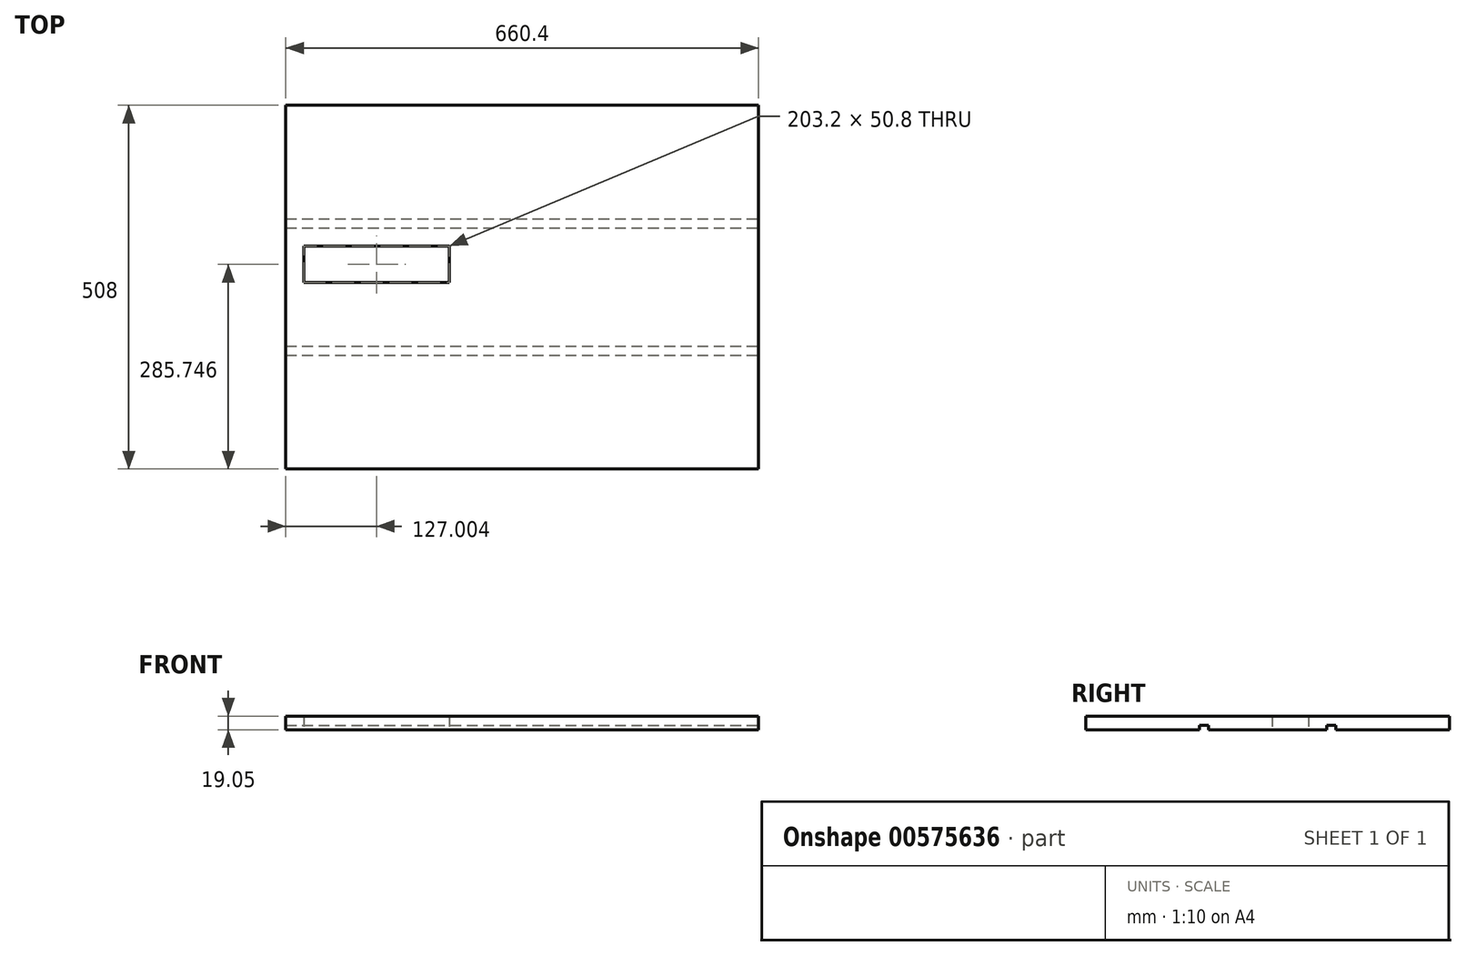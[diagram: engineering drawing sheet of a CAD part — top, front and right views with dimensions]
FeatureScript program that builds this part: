
annotation { "Feature Type Name" : "Feature", "Feature Type Description" : "" }
export const myFeature = defineFeature(function(context is Context, id is Id, definition is map)
    precondition{}
    {
        {
            var Q0;
            Q0=qCreatedBy(makeId("Top.planeOp"),FACE);
            var sketch = newSketch(context, id + "F0", { "sketchPlane" : qUnion([Q0])});
            skLineSegment(sketch, "E0.bottom", {"start": v(-46.34, 447.39) * mm, "end": v(614.06, 447.39) * mm});
            skLineSegment(sketch, "E0.top", {"start": v(-46.34, -60.61) * mm, "end": v(614.06, -60.61) * mm});
            skLineSegment(sketch, "E0.left", {"start": v(-46.34, 447.39) * mm, "end": v(-46.34, -60.61) * mm});
            skLineSegment(sketch, "E0.right", {"start": v(614.06, 447.39) * mm, "end": v(614.06, 415.64) * mm});
            skPoint(sketch, "E1.orphan", {"position": v(283.86, -60.61) * mm});
            skPoint(sketch, "E2.orphan", {"position": v(283.86, 447.39) * mm});
            skLineSegment(sketch, "E3.trimOffspring", {"start": v(614.06, 396.59) * mm, "end": v(614.06, -9.81) * mm});
            skLineSegment(sketch, "E4.trimOffspring", {"start": v(614.06, -28.86) * mm, "end": v(614.06, -60.61) * mm});
            skPoint(sketch, "E5.orphan", {"position": v(614.06, 193.39) * mm});
            skLineSegment(sketch, "E6", {"start": v(614.06, -9.81) * mm, "end": v(614.06, -28.86) * mm});
            skLineSegment(sketch, "E7", {"start": v(614.06, 396.59) * mm, "end": v(614.06, 415.64) * mm});
            skLineSegment(sketch, "E8", {"start": v(283.86, 447.39) * mm, "end": v(283.86, -60.61) * mm, "construction": true});
            skLineSegment(sketch, "E9.MirrorCS", {"start": v(182.26, 250.54) * mm, "end": v(182.26, 199.74) * mm});
            skLineSegment(sketch, "E10.MirrorCS", {"start": v(-20.94, 250.54) * mm, "end": v(182.26, 250.54) * mm});
            skLineSegment(sketch, "E11.MirrorCS", {"start": v(182.26, 199.74) * mm, "end": v(-20.94, 199.74) * mm});
            skLineSegment(sketch, "E12.MirrorCS", {"start": v(-20.94, 250.54) * mm, "end": v(-20.94, 199.74) * mm});
            skSolve(sketch);
        }
        {
            var Q0;
            Q0=qSketchRegion(id+"F0",true);
            extrude(context, id + "F1", {"entities" : qUnion([Q0]), "depth" : 19.05 * mm, "offsetDistance" : 25.4 * mm});
        }
        {
            var Q0;
            Q0=makeQuery(id+"F1.opExtrude","CAP_FACE",FACE,{"disambiguationData":[OSD([sQuery(id+"F0.wireOp",EDGE,"E0.bottom"),sQuery(id+"F0.wireOp",EDGE,"E0.top"),sQuery(id+"F0.wireOp",EDGE,"E0.left"),sQuery(id+"F0.wireOp",EDGE,"E0.right"),sQuery(id+"F0.wireOp",EDGE,"E3.trimOffspring"),sQuery(id+"F0.wireOp",EDGE,"E4.trimOffspring"),sQuery(id+"F0.wireOp",EDGE,"i5BfIIhn-vbHe-imx1-csDb-nMQiqM2HRBRM.top"),sQuery(id+"F0.wireOp",EDGE,"i5BfIIhn-vbHe-imx1-csDb-nMQiqM2HRBRM.right"),sQuery(id+"F0.wireOp",EDGE,"78bbb6ff-89c4-4b25-9ef8-bd1ca9e1b5700.MirrorCS"),sQuery(id+"F0.wireOp",EDGE,"78bbb6ff-89c4-4b25-9ef8-bd1ca9e1b5701.MirrorCS"),sQuery(id+"F0.wireOp",EDGE,"ff8e6387-9dfd-4042-92c4-0e13fc46f2381.MirrorCS"),sQuery(id+"F0.wireOp",EDGE,"ff8e6387-9dfd-4042-92c4-0e13fc46f2382.MirrorCS"),sQuery(id+"F0.wireOp",EDGE,"lPivuiSJ-rouK-T9NZ-5f0i-5M2m3eOQRDiC"),sQuery(id+"F0.wireOp",EDGE,"E6"),sQuery(id+"F0.wireOp",EDGE,"E7")])],"isStart":true});
            var sketch = newSketch(context, id + "F2", { "sketchPlane" : qUnion([Q0])});
            skLineSegment(sketch, "E13.bottom", {"start": v(-46.34, 60.61) * mm, "end": v(614.06, 60.61) * mm});
            skLineSegment(sketch, "E13.top", {"start": v(-46.34, -447.39) * mm, "end": v(614.06, -447.39) * mm});
            skLineSegment(sketch, "E13.left", {"start": v(-46.34, -98.14) * mm, "end": v(-46.34, -110.84) * mm});
            skLineSegment(sketch, "E13.right", {"start": v(614.06, -98.14) * mm, "end": v(614.06, -110.84) * mm});
            skLineSegment(sketch, "E14.0", {"start": v(4.46, -282.29) * mm, "end": v(614.06, -282.29) * mm, "construction": true});
            skLineSegment(sketch, "E15.0", {"start": v(-46.34, -104.49) * mm, "end": v(563.26, -104.49) * mm, "construction": true});
            skLineSegment(sketch, "E16.0", {"start": v(-46.34, -110.84) * mm, "end": v(614.06, -110.84) * mm});
            skLineSegment(sketch, "E17.0", {"start": v(-46.34, -98.14) * mm, "end": v(614.06, -98.14) * mm});
            skLineSegment(sketch, "E18.0", {"start": v(-46.34, -288.64) * mm, "end": v(614.06, -288.64) * mm});
            skLineSegment(sketch, "E19.0", {"start": v(-46.34, -275.94) * mm, "end": v(614.06, -275.94) * mm});
            skLineSegment(sketch, "E20.trimOffspring", {"start": v(614.06, -275.94) * mm, "end": v(614.06, -288.64) * mm});
            skLineSegment(sketch, "E21.trimOffspring", {"start": v(-46.34, -275.94) * mm, "end": v(-46.34, -288.64) * mm});
            skSolve(sketch);
        }
        {
            var Q0;
            {var subQ1=sQuery(id+"F2.wireOp",EDGE,"ede1b310-70a5-4bce-ad08-636cf6eacef5.0");Q0=makeQuery(id+"F2.imprint","IMPRINT",FACE,{"disambiguationData":[TD([[makeQuery(id+"F2.imprint","IMPRINT",EDGE,{"derivedFrom":subQ1}),1.0]])]});}
            var Q1;
            {var subQ3=sQuery(id+"F2.wireOp",EDGE,"b575b931-e8e5-4f5f-8ae3-ec7b51b93ddb.0");Q1=makeQuery(id+"F2.imprint","IMPRINT",FACE,{"disambiguationData":[TD([[makeQuery(id+"F2.imprint","IMPRINT",EDGE,{"derivedFrom":subQ3}),-1.0]])]});}
            var Q2;
            Q2=makeQuery(id+"F2.imprint","IMPRINT",FACE,{"disambiguationData":[TD([[makeQuery(id+"F2.imprint","IMPRINT",EDGE,{"derivedFrom":sQuery(id+"F2.wireOp",EDGE,"E18.0")}),1.0]])]});
            var Q3;
            Q3=makeQuery(id+"F2.imprint","IMPRINT",FACE,{"disambiguationData":[TD([[makeQuery(id+"F2.imprint","IMPRINT",EDGE,{"derivedFrom":sQuery(id+"F2.wireOp",EDGE,"E13.left")}),-1.0]])]});
            extrude(context, id + "F3", {"entities" : qUnion([Q0, Q1, Q2, Q3]), "operationType" : NewBodyOperationType.REMOVE, "oppositeDirection" : true, "depth" : 6.35 * mm, "offsetDistance" : 25.4 * mm});
        }
    });
